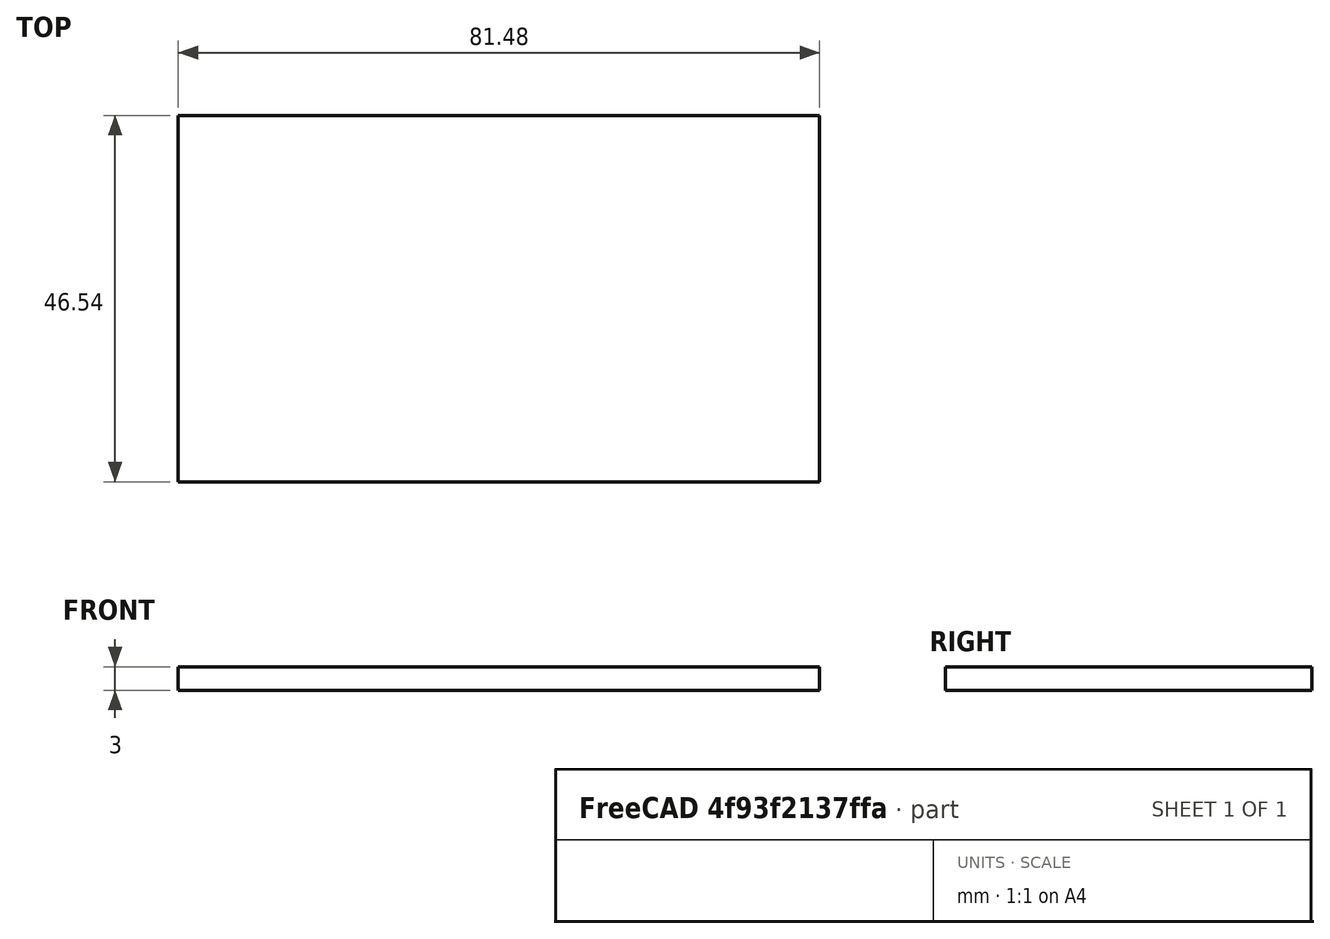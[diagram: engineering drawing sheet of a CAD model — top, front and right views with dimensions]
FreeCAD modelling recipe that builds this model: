
FCSTD DOCUMENT  (FreeCAD 0.19R24276 (Git))
Label: NewDesign
License: All rights reserved
LicenseURL: http://en.wikipedia.org/wiki/All_rights_reserved
objects: Sketcher::SketchObject×1, PartDesign::Pad×1, PartDesign::Body×1
note: 4 computed .brp shape members not serialized (recipe doc carries the construction recipe); baked Part::Feature solids carry a one-line shape summary decoded from their .brp

FEATURE [Sketcher::SketchObject] Sketch
  FullyConstrained = true
  MapMode = 5
  Support = -> [XY_Plane]
  sketch-geometry (4):
    g0: LineSegment StartX=0 StartY=0 StartZ=0 EndX=-81.48 EndY=0 EndZ=0
    g1: LineSegment StartX=-81.48 StartY=0 StartZ=0 EndX=-81.48 EndY=46.54 EndZ=0
    g2: LineSegment StartX=-81.48 StartY=46.54 StartZ=0 EndX=0 EndY=46.54 EndZ=0
    g3: LineSegment StartX=0 StartY=46.54 StartZ=0 EndX=0 EndY=0 EndZ=0
  constraints (11):
    c: Coincident(g0,g1)
    c: Coincident(g1,g2)
    c: Coincident(g2,g3)
    c: Coincident(g3,g0)
    c: Horizontal(g0)
    c: Horizontal(g2)
    c: Vertical(g1)
    c: Vertical(g3)
    c: Coincident(g0,g-1)
    c: DistanceX(g1,g2) = 81.48
    c: DistanceY(g0,g1) = 46.54
FEATURE [PartDesign::Pad] Pad
  Direction = (1,1,1)
  Length = 3
  Length2 = 100
  Profile = -> Sketch
  Type = 0
FEATURE [PartDesign::Body] Body
  Group = -> [Sketch,Pad]
  Origin = -> Origin
  Tip = -> Pad
